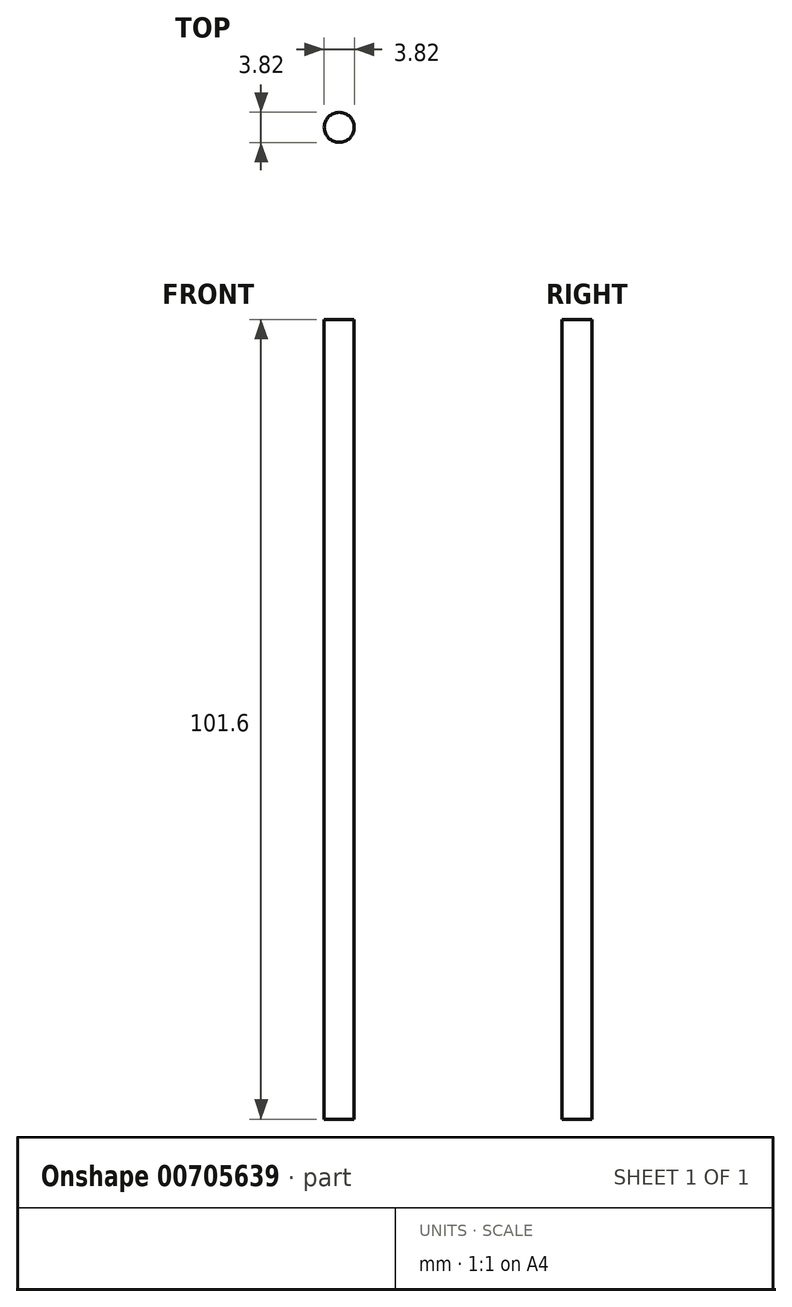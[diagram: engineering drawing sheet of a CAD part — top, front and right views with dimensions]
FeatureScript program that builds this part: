
annotation { "Feature Type Name" : "Feature", "Feature Type Description" : "" }
export const myFeature = defineFeature(function(context is Context, id is Id, definition is map)
    precondition{}
    {
        {
            var Q0;
            Q0=qCreatedBy(makeId("Top.planeOp"),FACE);
            var sketch = newSketch(context, id + "F0", { "sketchPlane" : qUnion([Q0])});
            skCircle(sketch, "E0", {"center": v(0, 0) * mm, "radius": 1.9 * mm});
            skSolve(sketch);
        }
        {
            var Q0;
            Q0=makeQuery(id+"F0.imprint","IMPRINT",FACE,{"disambiguationData":[TD([[makeQuery(id+"F0.imprint","IMPRINT",EDGE,{"derivedFrom":sQuery(id+"F0.wireOp",EDGE,"E0")}),1.0]])]});
            extrude(context, id + "F1", {"entities" : qUnion([Q0]), "depth" : 101.6 * mm, "offsetDistance" : 25.4 * mm});
        }
    });
